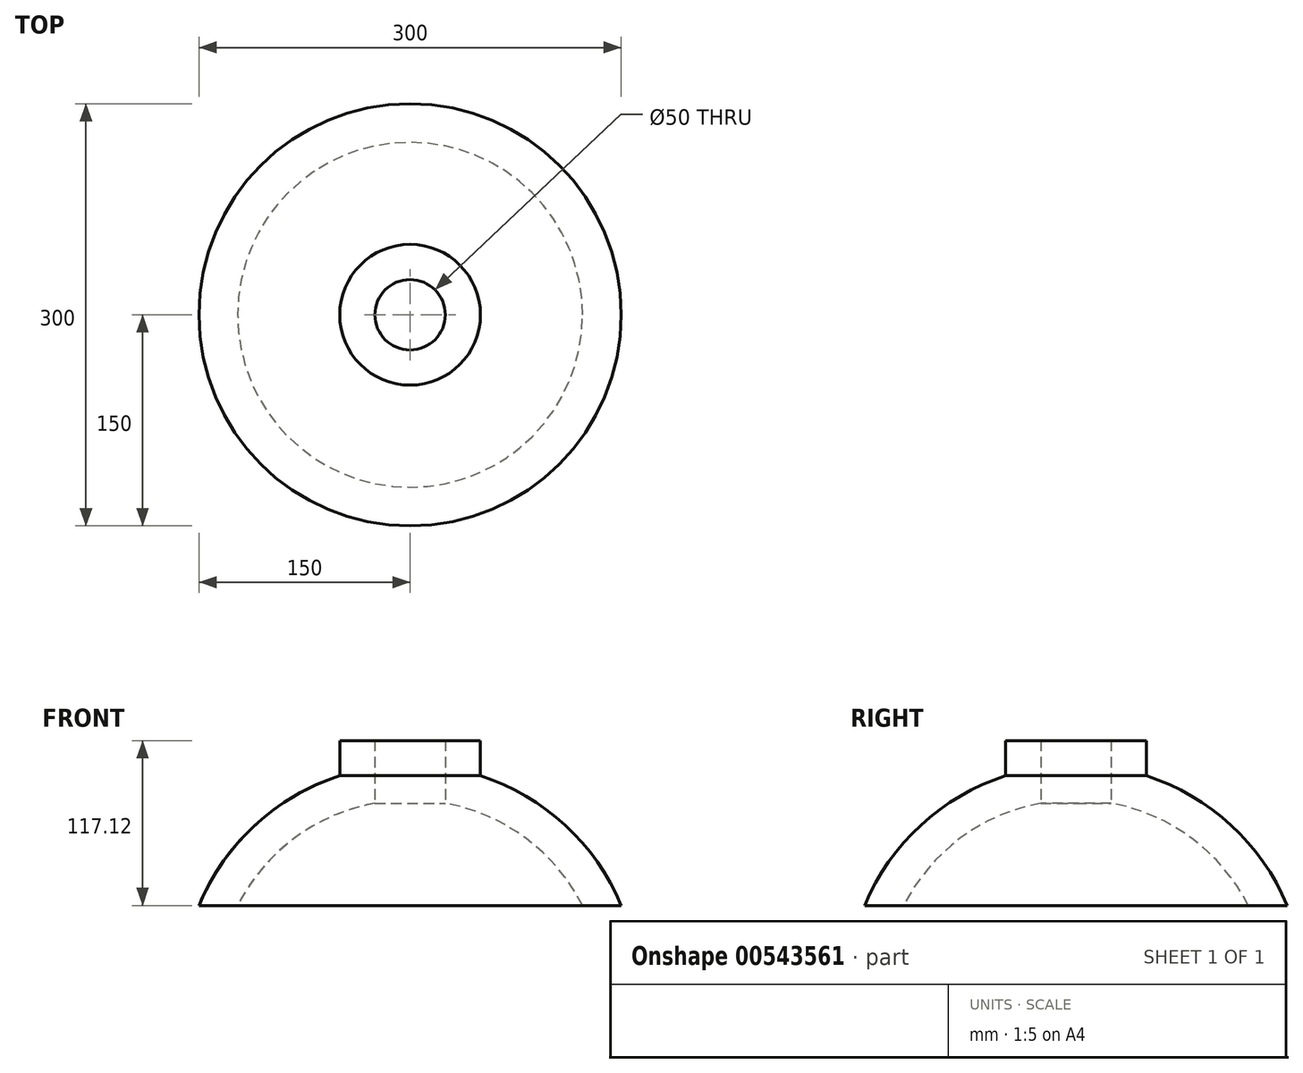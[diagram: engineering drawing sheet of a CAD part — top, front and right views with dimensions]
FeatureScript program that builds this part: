
annotation { "Feature Type Name" : "Feature", "Feature Type Description" : "" }
export const myFeature = defineFeature(function(context is Context, id is Id, definition is map)
    precondition{}
    {
        {
            var Q0;
            Q0=qCreatedBy(makeId("Front.planeOp"),FACE);
            var sketch = newSketch(context, id + "F0", { "sketchPlane" : qUnion([Q0])});
            skLineSegment(sketch, "E0", {"start": v(0, -81.08) * mm, "end": v(0, -62.5) * mm});
            skArc(sketch, "E1", {"start": v(150, 0) * mm, "mid": v(110.1, 57.02) * mm, "end": v(50, 92.12) * mm});
            skLineSegment(sketch, "E2.0", {"start": v(25, 72.7) * mm, "end": v(25, 117.12) * mm});
            skLineSegment(sketch, "E3.0", {"start": v(50, 92.12) * mm, "end": v(50, 117.12) * mm});
            skArc(sketch, "E4.0", {"start": v(122.47, 0) * mm, "mid": v(82.21, 47.72) * mm, "end": v(25, 72.7) * mm});
            skLineSegment(sketch, "E5", {"start": v(122.47, 0) * mm, "end": v(150, 0) * mm});
            skLineSegment(sketch, "E6.trimOffspring", {"start": v(0, 0) * mm, "end": v(0, 75) * mm});
            skPoint(sketch, "E7.orphan", {"position": v(0, 100) * mm});
            skLineSegment(sketch, "E8", {"start": v(50, 117.12) * mm, "end": v(25, 117.12) * mm});
            skSolve(sketch);
        }
        {
            var Q0;
            Q0 = qSketchRegion(id + "F0", true);
            var Q1;
            Q1=sQuery(id+"F0.wireOp",EDGE,"E6.trimOffspring");
            revolve(context, id + "F1", {"entities" : qUnion([Q0]), "axis" : qUnion([Q1]), "revolveType" : RevolveType.FULL});
        }
    });
